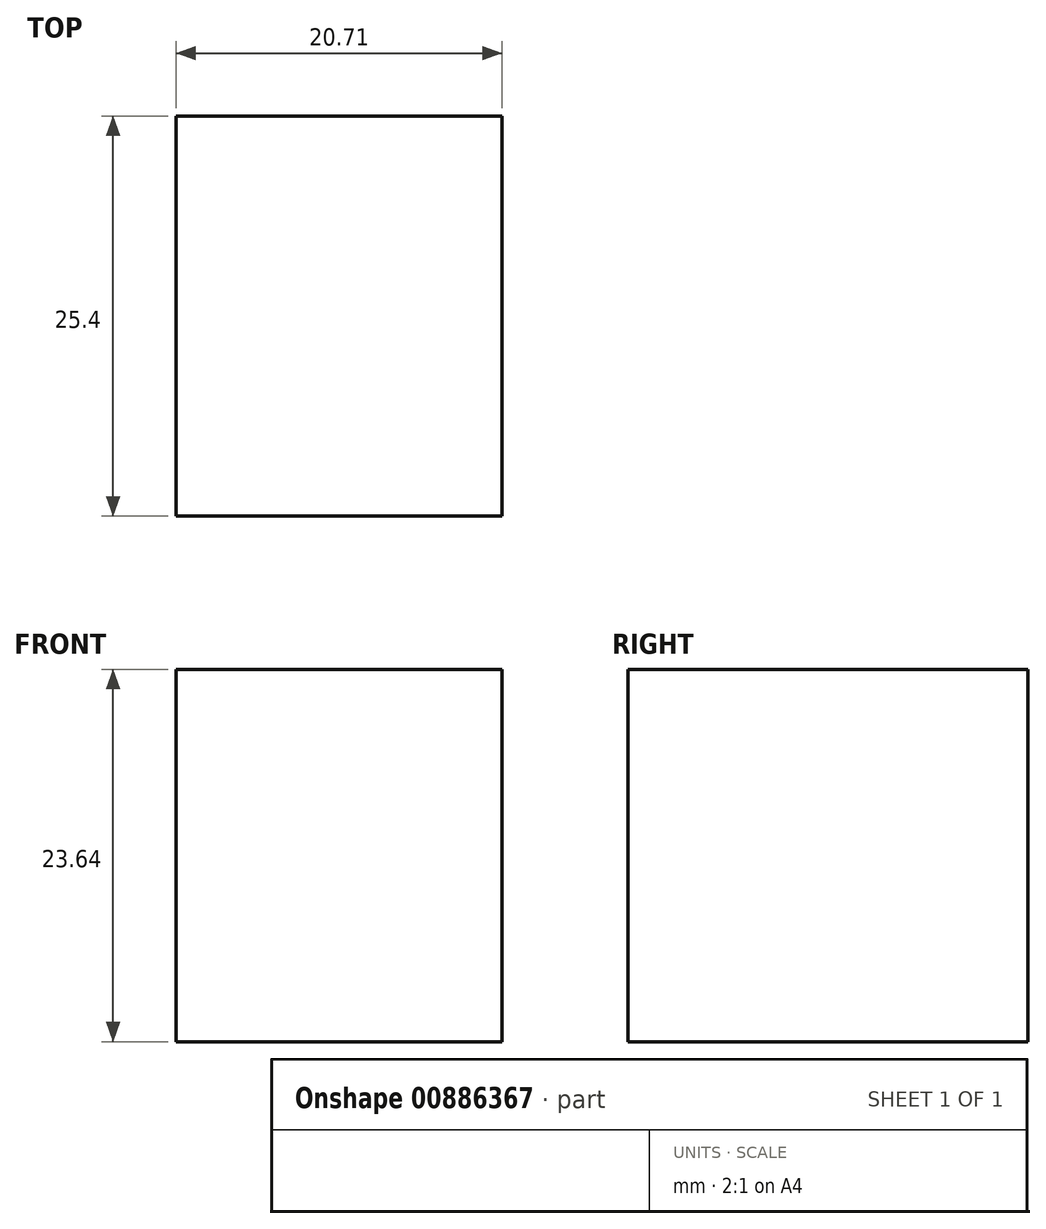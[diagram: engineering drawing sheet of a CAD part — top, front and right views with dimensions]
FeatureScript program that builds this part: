
annotation { "Feature Type Name" : "Feature", "Feature Type Description" : "" }
export const myFeature = defineFeature(function(context is Context, id is Id, definition is map)
    precondition{}
    {
        {
            var Q0;
            Q0=qCreatedBy(makeId("Front.planeOp"),FACE);
            var sketch = newSketch(context, id + "F0", { "sketchPlane" : qUnion([Q0])});
            skLineSegment(sketch, "E0.bottom", {"start": v(0, 0) * mm, "end": v(-20.71, 0) * mm});
            skLineSegment(sketch, "E0.top", {"start": v(0, 23.64) * mm, "end": v(-20.71, 23.64) * mm});
            skLineSegment(sketch, "E0.left", {"start": v(0, 0) * mm, "end": v(0, 23.64) * mm});
            skLineSegment(sketch, "E0.right", {"start": v(-20.71, 0) * mm, "end": v(-20.71, 23.64) * mm});
            skSolve(sketch);
        }
        {
            var Q0;
            Q0 = qSketchRegion(id + "F0", true);
            extrude(context, id + "F1", {"entities" : qUnion([Q0]), "depth" : 25.4 * mm, "offsetDistance" : 25.4 * mm});
        }
    });
